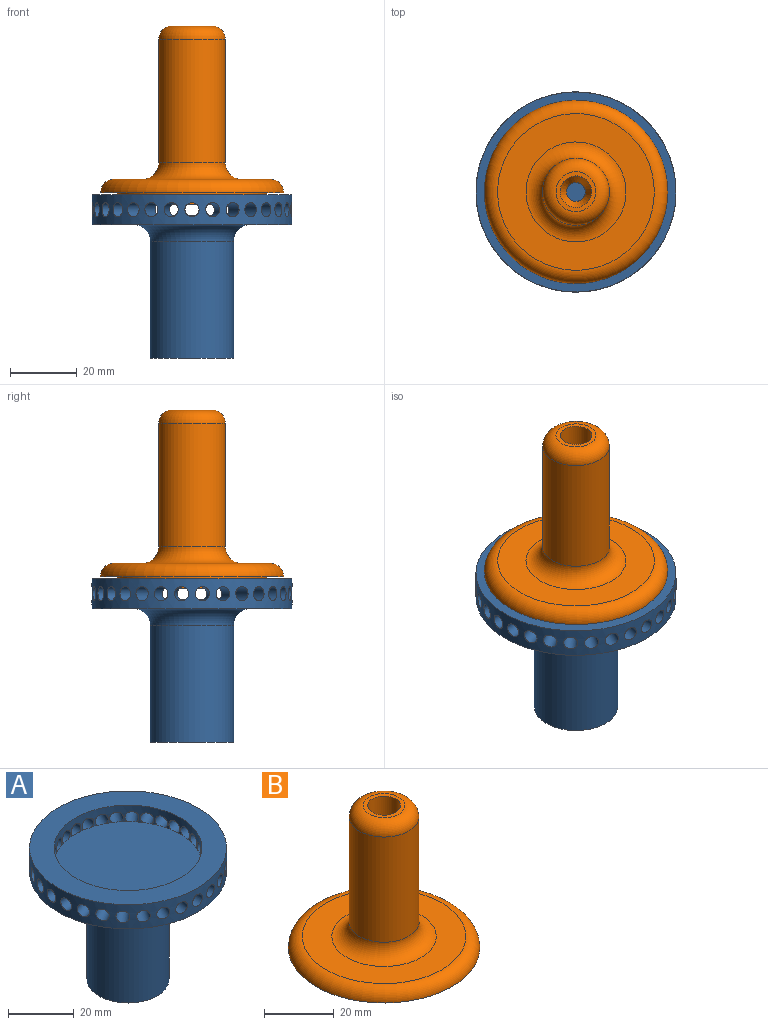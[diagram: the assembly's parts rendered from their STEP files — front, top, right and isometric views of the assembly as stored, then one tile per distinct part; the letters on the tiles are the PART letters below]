
ASSEMBLY  parts=2 mates=1
PART A: 70 faces, bbox 60.1x60x49 mm
  f0: cylinder r=22.5mm len=45mm, axis (0,0,1), area 467.5mm2, adj f1,f2,f3,f4,f5,f6,f7,f8
  f1: cylinder r=2.12mm len=8.32mm, axis (-0.21,-0.98,0), area 100.3mm2, adj f0,f34,f39
  f2: cylinder r=2.12mm len=8.67mm, axis (-0.41,-0.91,0), area 100.3mm2, adj f0,f34,f40
  f3: cylinder r=2.12mm len=8.65mm, axis (-0.59,-0.81,0), area 100.3mm2, adj f0,f34,f41
  f4: cylinder r=2.12mm len=8.49mm, axis (-0.74,-0.67,0), area 100.3mm2, adj f0,f34,f42
  f5: cylinder r=2.12mm len=8.71mm, axis (-0.87,-0.5,0), area 100.3mm2, adj f0,f34,f43
  f6: cylinder r=2.12mm len=8.54mm, axis (-0.95,-0.31,0), area 100.3mm2, adj f0,f34,f44
  f7: cylinder r=2.12mm len=8mm, axis (-0.99,-0.1,0), area 100.3mm2, adj f0,f34,f45
  f8: cylinder r=2.12mm len=8mm, axis (-0.99,0.1,0), area 100.3mm2, adj f0,f34,f46
  f9: cylinder r=2.12mm len=8.54mm, axis (-0.95,0.31,0), area 100.3mm2, adj f0,f34,f47
  f10: cylinder r=2.12mm len=8.71mm, axis (-0.87,0.5,0), area 100.3mm2, adj f0,f34,f48
  f11: cylinder r=2.12mm len=8.49mm, axis (-0.74,0.67,0), area 100.3mm2, adj f0,f34,f49
  f12: cylinder r=2.12mm len=8.65mm, axis (-0.59,0.81,0), area 100.3mm2, adj f0,f34,f50
  f13: cylinder r=2.12mm len=8.67mm, axis (-0.41,0.91,0), area 100.3mm2, adj f0,f34,f51
  f14: cylinder r=2.12mm len=8.32mm, axis (-0.21,0.98,0), area 100.3mm2, adj f0,f34,f52
  f15: cylinder r=2.12mm len=7.6mm, axis (0,1,0), area 100.3mm2, adj f0,f34,f53
  f16: cylinder r=2.12mm len=8.32mm, axis (0.21,0.98,0), area 100.3mm2, adj f0,f34,f54
  f17: cylinder r=2.12mm len=8.67mm, axis (0.41,0.91,0), area 100.3mm2, adj f0,f34,f55
  f18: cylinder r=2.12mm len=8.65mm, axis (0.59,0.81,0), area 100.3mm2, adj f0,f34,f56
  f19: cylinder r=2.12mm len=8.49mm, axis (0.74,0.67,0), area 100.3mm2, adj f0,f34,f57
  f20: cylinder r=2.12mm len=8.71mm, axis (0.87,0.5,0), area 100.3mm2, adj f0,f34,f58
  f21: cylinder r=2.12mm len=8.54mm, axis (0.95,0.31,0), area 100.3mm2, adj f0,f34,f59
  f22: cylinder r=2.12mm len=8mm, axis (0.99,0.1,0), area 100.3mm2, adj f0,f34,f60
  f23: cylinder r=2.12mm len=8mm, axis (0.99,-0.1,0), area 100.3mm2, adj f0,f34,f61
  f24: cylinder r=2.12mm len=8.54mm, axis (0.95,-0.31,0), area 100.3mm2, adj f0,f34,f62
  f25: cylinder r=2.12mm len=8.71mm, axis (0.87,-0.5,0), area 100.3mm2, adj f0,f34,f63
  f26: cylinder r=2.12mm len=8.49mm, axis (0.74,-0.67,0), area 100.3mm2, adj f0,f34,f64
  f27: cylinder r=2.12mm len=8.65mm, axis (0.59,-0.81,0), area 100.3mm2, adj f0,f34,f65
  f28: cylinder r=2.12mm len=8.67mm, axis (0.41,-0.91,0), area 100.3mm2, adj f0,f34,f66
  f29: cylinder r=2.12mm len=8.32mm, axis (0.21,-0.98,0), area 100.3mm2, adj f0,f34,f67
  f30: cylinder r=4.1mm len=30mm, axis (0,0,-1), area 772.8mm2, adj f32,f33
  f31: cylinder r=12.5mm len=35mm, axis (0,0,-1), area 2748.9mm2, adj f32,f38
  f32: plane 25x25mm, normal (0,0,-1), area 438.1mm2, adj f30,f31
  f33: plane 8.2x8.2mm, normal (0,0,-1), area 52.8mm2, adj f30
  f34: cylinder r=30mm len=60mm, axis (0,0,-1), area 1269.7mm2, adj f1,f2,f3,f4,f5,f6,f7,f8
  f35: plane 60x60mm, normal (0,0,1), area 1237mm2, adj f0,f34
  f36: plane 60x60mm, normal (0,0,-1), area 1865.3mm2, adj f34,f38
  f37: cylinder r=2.12mm len=7.6mm, axis (0,-1,0), area 100.3mm2, adj f0,f34,f68
  f38: torus R=17.5mm, axis (0,0,1), area 706.5mm2, adj f31,f36
  f39: cylinder r=22.5mm len=2.68mm, axis (0,0,-1), area 0.9mm2, adj f1,f69
  f40: cylinder r=22.5mm len=2.5mm, axis (0,0,-1), area 0.9mm2, adj f2,f69
  f41: cylinder r=22.5mm len=2.22mm, axis (0,0,-1), area 0.9mm2, adj f3,f69
  f42: cylinder r=22.5mm len=2.04mm, axis (0,0,-1), area 0.9mm2, adj f4,f69
  f43: cylinder r=22.5mm len=2.37mm, axis (0,0,-1), area 0.9mm2, adj f5,f69
  f44: cylinder r=22.5mm len=2.6mm, axis (0,0,-1), area 0.9mm2, adj f6,f69
  f45: cylinder r=22.5mm len=2.72mm, axis (0,0,-1), area 0.9mm2, adj f7,f69
  f46: cylinder r=22.5mm len=2.72mm, axis (0,0,-1), area 0.9mm2, adj f8,f69
  f47: cylinder r=22.5mm len=2.6mm, axis (0,0,-1), area 0.9mm2, adj f9,f69
  f48: cylinder r=22.5mm len=2.37mm, axis (0,0,-1), area 0.9mm2, adj f10,f69
  f49: cylinder r=22.5mm len=2.04mm, axis (0,0,-1), area 0.9mm2, adj f11,f69
  f50: cylinder r=22.5mm len=2.22mm, axis (0,0,-1), area 0.9mm2, adj f12,f69
  f51: cylinder r=22.5mm len=2.5mm, axis (0,0,-1), area 0.9mm2, adj f13,f69
  f52: cylinder r=22.5mm len=2.68mm, axis (0,0,-1), area 0.9mm2, adj f14,f69
  f53: cylinder r=22.5mm len=2.74mm, axis (0,0,-1), area 0.9mm2, adj f15,f69
  f54: cylinder r=22.5mm len=2.68mm, axis (0,0,-1), area 0.9mm2, adj f16,f69
  f55: cylinder r=22.5mm len=2.5mm, axis (0,0,-1), area 0.9mm2, adj f17,f69
  f56: cylinder r=22.5mm len=2.22mm, axis (0,0,-1), area 0.9mm2, adj f18,f69
  f57: cylinder r=22.5mm len=2.04mm, axis (0,0,-1), area 0.9mm2, adj f19,f69
  f58: cylinder r=22.5mm len=2.37mm, axis (0,0,-1), area 0.9mm2, adj f20,f69
  f59: cylinder r=22.5mm len=2.6mm, axis (0,0,-1), area 0.9mm2, adj f21,f69
  f60: cylinder r=22.5mm len=2.72mm, axis (0,0,-1), area 0.9mm2, adj f22,f69
  f61: cylinder r=22.5mm len=2.72mm, axis (0,0,-1), area 0.9mm2, adj f23,f69
  f62: cylinder r=22.5mm len=2.6mm, axis (0,0,-1), area 0.9mm2, adj f24,f69
  f63: cylinder r=22.5mm len=2.37mm, axis (0,0,-1), area 0.9mm2, adj f25,f69
  f64: cylinder r=22.5mm len=2.04mm, axis (0,0,-1), area 0.9mm2, adj f26,f69
  f65: cylinder r=22.5mm len=2.22mm, axis (0,0,-1), area 0.9mm2, adj f27,f69
  f66: cylinder r=22.5mm len=2.5mm, axis (0,0,-1), area 0.9mm2, adj f28,f69
  f67: cylinder r=22.5mm len=2.68mm, axis (0,0,-1), area 0.9mm2, adj f29,f69
  f68: cylinder r=22.5mm len=2.74mm, axis (0,0,-1), area 0.9mm2, adj f37,f69
  f69: plane 45x45mm, normal (0,0,1), area 1590.4mm2, adj f0,f39,f40,f41,f42,f43,f44,f45
PART B: 12 faces, bbox 59.5x59.5x53.5 mm
  f0: cylinder r=4.72mm len=44.53mm, axis (0,0,-1), area 1321.9mm2, adj f2,f7
  f1: cylinder r=10mm len=37mm, axis (0,0,-1), area 2324.8mm2, adj f5,f11
  f2: plane 12x12mm, normal (0,0,1), area 43mm2, adj f0,f5
  f3: cylinder r=22.43mm len=44.85mm, axis (0,0,1), area 493.2mm2, adj f4,f9
  f4: plane 44.85x44.85mm, normal (0,0,-1), area 1555.2mm2, adj f3,f6
  f5: torus R=6mm, axis (0,0,1), area 337.4mm2, adj f1,f2
  f6: cylinder r=2.8mm len=5.6mm, axis (0,0,-1), area 80.9mm2, adj f4,f7
  f7: cone r=5mm half-angle=23.7deg, axis (0,0,1), area 113mm2, adj f0,f6
  f8: plane 47x47mm, normal (0,0,1), area 1028.1mm2, adj f10,f11
  f9: plane 55x55mm, normal (0,0,-1), area 796mm2, adj f3,f10
  f10: torus R=23.5mm, axis (0,0,1), area 1028.3mm2, adj f8,f9
  f11: torus R=15mm, axis (0,0,1), area 583.1mm2, adj f1,f8
PLACE A t=(27.17,53.68,-16.16)mm
PLACE B t=(27.17,53.68,33.41)mm
MATE fastened A.f0 <-> B.f6  axis (0,0,1) through (27.17,53.68,29.91)mm
